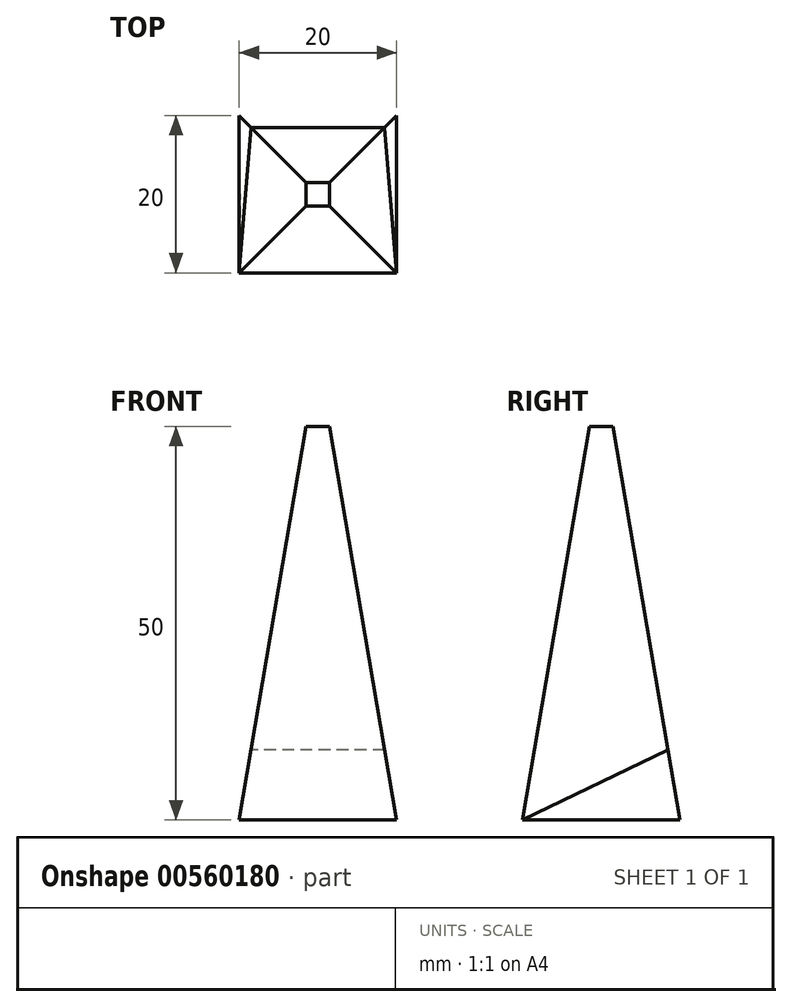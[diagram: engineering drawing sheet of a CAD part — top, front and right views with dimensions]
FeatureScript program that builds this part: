
annotation { "Feature Type Name" : "Feature", "Feature Type Description" : "" }
export const myFeature = defineFeature(function(context is Context, id is Id, definition is map)
    precondition{}
    {
        {
            var Q0;
            Q0=qCreatedBy(makeId("Top.planeOp"),FACE);
            cPlane(context, id + "F0", {"entities" : qUnion([Q0]), "cplaneType" : CPlaneType.OFFSET, "offset" : 50 * mm, "width" : 152.4 * mm, "height" : 152.4 * mm});
        }
        {
            var Q0;
            Q0=qCreatedBy(makeId("Top.planeOp"),FACE);
            var sketch = newSketch(context, id + "F1", { "sketchPlane" : qUnion([Q0])});
            skLineSegment(sketch, "E0.bottom", {"start": v(-10, 10) * mm, "end": v(10, 10) * mm});
            skLineSegment(sketch, "E0.top", {"start": v(-10, -10) * mm, "end": v(10, -10) * mm});
            skLineSegment(sketch, "E0.left", {"start": v(-10, 10) * mm, "end": v(-10, -10) * mm});
            skLineSegment(sketch, "E0.right", {"start": v(10, 10) * mm, "end": v(10, -10) * mm});
            skPoint(sketch, "E0.middle", {"position": v(0, 0) * mm});
            skSolve(sketch);
        }
        {
            var Q0;
            Q0=qCreatedBy(id+"F0.planeOp",FACE);
            var sketch = newSketch(context, id + "F2", { "sketchPlane" : qUnion([Q0])});
            skLineSegment(sketch, "E1.bottom", {"start": v(-1.5, 1.5) * mm, "end": v(1.5, 1.5) * mm});
            skLineSegment(sketch, "E1.top", {"start": v(-1.5, -1.5) * mm, "end": v(1.5, -1.5) * mm});
            skLineSegment(sketch, "E1.left", {"start": v(-1.5, 1.5) * mm, "end": v(-1.5, -1.5) * mm});
            skLineSegment(sketch, "E1.right", {"start": v(1.5, 1.5) * mm, "end": v(1.5, -1.5) * mm});
            skPoint(sketch, "E1.middle", {"position": v(0, 0) * mm});
            skSolve(sketch);
        }
        {
            var Q0;
            Q0=makeQuery(id+"F1.imprint","IMPRINT",FACE,{"disambiguationData":[TD([[makeQuery(id+"F1.imprint","IMPRINT",EDGE,{"derivedFrom":sQuery(id+"F1.wireOp",EDGE,"E0.bottom")}),-1.0]])]});
            var Q1;
            Q1=makeQuery(id+"F2.imprint","IMPRINT",FACE,{"disambiguationData":[TD([[makeQuery(id+"F2.imprint","IMPRINT",EDGE,{"derivedFrom":sQuery(id+"F2.wireOp",EDGE,"E1.bottom")}),-1.0]])]});
            loft(context, id + "F3", {"sheetProfilesArray" : [{ "sheetProfileEntities" : qUnion([Q0]) }, { "sheetProfileEntities" : qUnion([Q1]) }]});
        }
        {
            var Q0;
            Q0=makeQuery(id+"F3.opLoft","SWEPT_FACE",FACE,{"disambiguationData":[OSD([sQuery(id+"F1.wireOp",EDGE,"E0.bottom"),sQuery(id+"F1.wireOp",EDGE,"E0.left"),sQuery(id+"F1.wireOp",EDGE,"E0.right"),sQuery(id+"F2.wireOp",EDGE,"E1.bottom"),sQuery(id+"F2.wireOp",EDGE,"E1.left"),sQuery(id+"F2.wireOp",EDGE,"E1.right")])]});
            var sketch = newSketch(context, id + "F4", { "sketchPlane" : qUnion([Q0])});
            skLineSegment(sketch, "E2.bottom", {"start": v(-15.5, 7.35) * mm, "end": v(17.8, 7.35) * mm});
            skLineSegment(sketch, "E2.top", {"start": v(-15.5, -4.1) * mm, "end": v(17.8, -4.1) * mm});
            skLineSegment(sketch, "E2.left", {"start": v(-15.5, 7.35) * mm, "end": v(-15.5, -4.1) * mm});
            skLineSegment(sketch, "E2.right", {"start": v(17.8, 7.35) * mm, "end": v(17.8, -4.1) * mm});
            skSolve(sketch);
        }
        {
            var Q0;
            Q0=makeQuery(id+"F3.opLoft","SWEPT_FACE",FACE,{"disambiguationData":[OSD([sQuery(id+"F1.wireOp",EDGE,"E0.top"),sQuery(id+"F1.wireOp",EDGE,"E0.left"),sQuery(id+"F1.wireOp",EDGE,"E0.right"),sQuery(id+"F2.wireOp",EDGE,"E1.top"),sQuery(id+"F2.wireOp",EDGE,"E1.left"),sQuery(id+"F2.wireOp",EDGE,"E1.right")])]});
            var sketch = newSketch(context, id + "F5", { "sketchPlane" : qUnion([Q0])});
            skLineSegment(sketch, "E3.bottom", {"start": v(10, -1.68) * mm, "end": v(-10, -1.68) * mm});
            skLineSegment(sketch, "E3.top", {"start": v(10, -2.75) * mm, "end": v(-10, -2.75) * mm});
            skLineSegment(sketch, "E3.left", {"start": v(10, -1.68) * mm, "end": v(10, -2.75) * mm});
            skLineSegment(sketch, "E3.right", {"start": v(-10, -1.68) * mm, "end": v(-10, -2.75) * mm});
            skSolve(sketch);
        }
        {
            var Q1;
            Q1=makeQuery(id+"F5.imprint","IMPRINT",FACE,{"disambiguationData":[TD([[makeQuery(id+"F5.imprint","IMPRINT",EDGE,{"derivedFrom":sQuery(id+"F5.wireOp",EDGE,"E3.bottom")}),-1.0]])]});
            var Q2;
            {var subQ2=sQuery(id+"F1.wireOp",EDGE,"E0.right");var subQ3=sQuery(id+"F1.wireOp",EDGE,"E0.bottom");var subQ6=sQuery(id+"F1.wireOp",EDGE,"E0.left");var subQ9=makeQuery(id+"F3.opLoft","MID_CAP_EDGE",EDGE,{"disambiguationData":[OSD([subQ3,subQ6,subQ2])],"capPos":0.0});Q2=makeQuery(id+"F4.imprint","IMPRINT",FACE,{"disambiguationData":[TD([[makeQuery(id+"F4.imprint","IMPRINT",EDGE,{"derivedFrom":subQ9}),1.0]])]});}
            loft(context, id + "F6", {"operationType" : NewBodyOperationType.REMOVE, "sheetProfilesArray" : [{ "sheetProfileEntities" : qUnion([Q1]) }, { "sheetProfileEntities" : qUnion([Q2]) }]});
        }
    });
